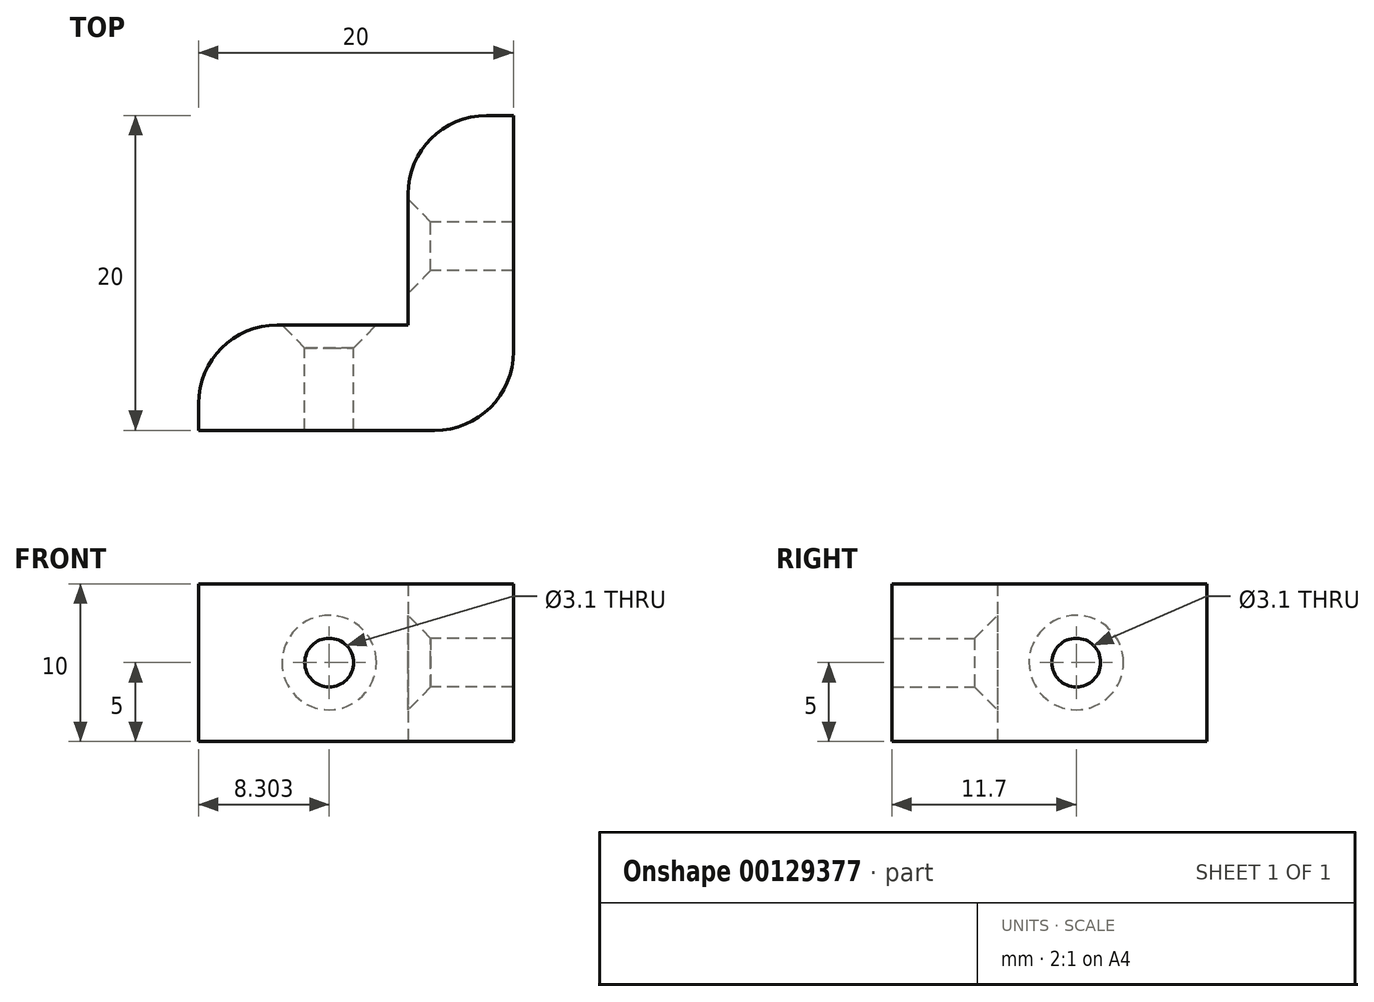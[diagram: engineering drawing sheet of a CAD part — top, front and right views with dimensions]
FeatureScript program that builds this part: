
annotation { "Feature Type Name" : "Feature", "Feature Type Description" : "" }
export const myFeature = defineFeature(function(context is Context, id is Id, definition is map)
    precondition{}
    {
        {
            var Q0;
            Q0=qCreatedBy(makeId("Top.planeOp"),FACE);
            var sketch = newSketch(context, id + "F0", { "sketchPlane" : qUnion([Q0])});
            skLineSegment(sketch, "E0", {"start": v(-37.67, 0) * mm, "end": v(-17.67, 0) * mm});
            skLineSegment(sketch, "E1", {"start": v(-17.67, 0) * mm, "end": v(-17.67, 20) * mm});
            skLineSegment(sketch, "E2", {"start": v(-37.67, 0) * mm, "end": v(-37.67, 6.7) * mm});
            skLineSegment(sketch, "E3", {"start": v(-37.67, 6.7) * mm, "end": v(-24.37, 6.7) * mm});
            skLineSegment(sketch, "E4", {"start": v(-24.37, 6.7) * mm, "end": v(-24.37, 20) * mm});
            skLineSegment(sketch, "E5", {"start": v(-24.37, 20) * mm, "end": v(-17.67, 20) * mm});
            skSolve(sketch);
        }
        {
            var Q0;
            Q0=makeQuery(id+"F0.imprint","IMPRINT",FACE,{"disambiguationData":[TD([[makeQuery(id+"F0.imprint","IMPRINT",EDGE,{"derivedFrom":sQuery(id+"F0.wireOp",EDGE,"E0")}),1.0]])]});
            extrude(context, id + "F1", {"entities" : qUnion([Q0]), "endBound" : BoundingType.SYMMETRIC, "depth" : 10 * mm});
        }
        {
            var Q0;
            Q0=makeQuery(id+"F1.opExtrude","SWEPT_FACE",FACE,{"disambiguationData":[OSD([sQuery(id+"F0.wireOp",EDGE,"E4")])]});
            var sketch = newSketch(context, id + "F2", { "sketchPlane" : qUnion([Q0])});
            skPoint(sketch, "E6", {"position": v(-11.7, 0) * mm});
            skSolve(sketch);
        }
        {
            var Q0;
            Q0=makeQuery(id+"F1.opExtrude","SWEPT_FACE",FACE,{"disambiguationData":[OSD([sQuery(id+"F0.wireOp",EDGE,"E3")])]});
            var sketch = newSketch(context, id + "F3", { "sketchPlane" : qUnion([Q0])});
            skPoint(sketch, "E7", {"position": v(29.37, 0) * mm});
            skSolve(sketch);
        }
        {
            var Q0;
            Q0=sQuery(id+"F2.wireOp",VERTEX,"E6");
            var Q1;
            Q1=makeQuery(id+"F1.opExtrude","SWEPT_BODY",BODY,{"disambiguationData":[OSD([sQuery(id+"F0.wireOp",EDGE,"E0"),sQuery(id+"F0.wireOp",EDGE,"E1"),sQuery(id+"F0.wireOp",EDGE,"E2"),sQuery(id+"F0.wireOp",EDGE,"E3"),sQuery(id+"F0.wireOp",EDGE,"E4"),sQuery(id+"F0.wireOp",EDGE,"E5")])]});
            hole(context, id + "F4", {"style" : HoleStyle.C_SINK, "endStyle" : HoleEndStyle.THROUGH, "holeDiameter" : 3.1 * mm, "cSinkDiameter" : 6 * mm, "cSinkAngle" : 90 * degree, "startFromSketch" : true, "locations" : qUnion([Q0]), "scope" : qUnion([Q1]), "isTappedThrough" : true});
        }
        {
            var Q0;
            Q0=sQuery(id+"F3.wireOp",VERTEX,"E7");
            var Q1;
            Q1=makeQuery(id+"F1.opExtrude","SWEPT_BODY",BODY,{"disambiguationData":[OSD([sQuery(id+"F0.wireOp",EDGE,"E0"),sQuery(id+"F0.wireOp",EDGE,"E1"),sQuery(id+"F0.wireOp",EDGE,"E2"),sQuery(id+"F0.wireOp",EDGE,"E3"),sQuery(id+"F0.wireOp",EDGE,"E4"),sQuery(id+"F0.wireOp",EDGE,"E5")])]});
            hole(context, id + "F5", {"style" : HoleStyle.C_SINK, "endStyle" : HoleEndStyle.THROUGH, "holeDiameter" : 3.1 * mm, "cSinkDiameter" : 6 * mm, "cSinkAngle" : 90 * degree, "startFromSketch" : true, "locations" : qUnion([Q0]), "scope" : qUnion([Q1]), "isTappedThrough" : true});
        }
        {
            var Q0;
            Q0=makeQuery(id+"F1.opExtrude","SWEPT_EDGE",EDGE,{"disambiguationData":[OSD([sQuery(id+"F0.wireOp",EDGE,"E0"),sQuery(id+"F0.wireOp",EDGE,"E1")])]});
            fillet(context, id + "F6", {"entities" : qUnion([Q0]), "radius" : 5 * mm, "tangentPropagation" : true, "allowEdgeOverflow" : false});
        }
        {
            var Q0;
            Q0=makeQuery(id+"F1.opExtrude","SWEPT_EDGE",EDGE,{"disambiguationData":[OSD([sQuery(id+"F0.wireOp",EDGE,"E4"),sQuery(id+"F0.wireOp",EDGE,"E5")])]});
            var Q1;
            Q1=makeQuery(id+"F1.opExtrude","SWEPT_EDGE",EDGE,{"disambiguationData":[OSD([sQuery(id+"F0.wireOp",EDGE,"E2"),sQuery(id+"F0.wireOp",EDGE,"E3")])]});
            fillet(context, id + "F7", {"entities" : qUnion([Q0, Q1]), "radius" : 5 * mm, "tangentPropagation" : true, "allowEdgeOverflow" : false});
        }
    });
